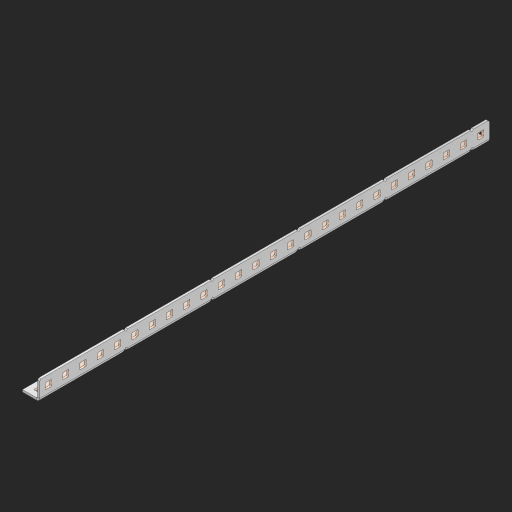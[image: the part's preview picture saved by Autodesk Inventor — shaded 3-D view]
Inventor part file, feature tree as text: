
AUTODESK INVENTOR PART (.ipt)
format: ipt  version: 2023 (Build 270158000, 158)  size: 886,272 bytes
history: native  units: in
note: dims shown in document units (in); Inventor stores cm internally (conversion verified against a paired STEP export)
features: other x57, extrude x51, sheet_metal_op x10, sketch x8, mirror x1, pattern_linear x1, chamfer x1
ambient origin geometry x8: Origin, YZ Plane, XZ Plane, XY Plane, X Axis, Y Axis, Z Axis, Center Point
bodies: Solid1 (feature_tree), Body (feature_tree)
feature tree (129):
  other  "Flange Pattern Plane"
  sheet_metal_op  "Flange Pattern"
  sheet_metal_op  "Body Pattern"
  other  "Arc Length"
  mirror  "Notch Mirror"
  pattern_linear  "Notch Pattern"  Spacing1=0.25in  [1 undecoded]
  chamfer  "End Chamfer"
  extrude  "Half Cut"  Depth=0.0625in
  sketch  "Sketch1"  dims[d0=1.5in]
  other  "Plate1"
  sketch  "Sketch2"  dims[d1=13.0in]
  other  "Plate2"
  sheet_metal_op  "Bend1"
  sheet_metal_op  "Corner1"
  sketch  "Sketch3"  dims[d2=0.0625in]
  other  "Flange Pattern Sketch"
  sketch  "Sketch7"  dims[d3=0.0625in]
  other  "Srf1"
  other  "Srf2"
  sketch  "Sketch8"  dims[d4=0.0312in]
  sketch  "Sketch9"  dims[d5=0.125in]
  other  "Srf91"
  sheet_metal_op  "Body Pattern Sketch"
  other  "Srf92"
  sketch  "Sketch13"  dims[d6=0.0625in]
  sketch  "Sketch14"  dims[d7=0.5in d8=90.0deg d9=0.0312in d10=0.25in d11=0.0625in d12=0.0625in d16=0.182in d17=0.02in d18=0.0625in d19=0.0in d20=0.25in d21=0.25in d46=0.172in d47=1.0in d48=0.0in d49=0.182in d50=0.02in d51=0.25in d52=0.25in d53=0.0625in d54=0.0in d55=0.172in d56=1.0in d57=0.0in d60=10.2362in d62=0.5in d63=0.3937in d65=0.5in d85=0.1473in d86=0.1782in d88=0.04in d89=0.0625in d90=0.0in d91=0.04in d92=0.0491in d95=2.5in d96=0.04in d97=0.25in d98=45.0deg d101=0.0in d102=2.497in d131=0.5in d132=10.2362in d134=0.5in d139=0.5in]
  other  "Srf856"
  other  "Srf1310"
  other  "Srf1311"
  other  "Srf1312"
  other  "Srf1376"
  other  "Srf1377"
  other  "Srf1728"
  other  "Srf1755"
  other  "Srf1878"
  other  "Srf1879"
  other  "Srf1880"
  other  "Srf1881"
  other  "Srf1882"
  other  "Srf1883"
  other  "Srf1884"
  other  "Srf1885"
  other  "Srf1886"
  other  "Srf1887"
  other  "Srf1888"
  other  "Srf1889"
  other  "Srf1890"
  other  "Srf1891"
  other  "Srf1892"
  other  "Srf1893"
  other  "Srf1894"
  other  "Srf1895"
  other  "Srf1896"
  other  "Srf1897"
  other  "Srf1942"
  other  "Srf1943"
  other  "Srf1944"
  other  "Srf1945"
  other  "Srf1946"
  other  "Srf1947"
  other  "Srf1948"
  other  "Srf1949"
  other  "Srf1950"
  other  "Srf1951"
  other  "Srf1952"
  other  "Srf1953"
  other  "Srf1954"
  other  "Srf1955"
  other  "Srf1956"
  other  "Srf1957"
  other  "Srf1958"
  other  "Srf1959"
  other  "Srf1960"
  other  "Srf1961"
  sheet_metal_op  "Flange Stamp"
  sheet_metal_op  "Flange Circle"
  sheet_metal_op  "Body Stamp"
  sheet_metal_op  "Body Circle"
  sheet_metal_op  "Notch"
  extrude  "ExtrusionSrf2"  Depth=0.0625in
  extrude  "ExtrusionSrf92"  Depth=0.5in
  extrude  "ExtrusionSrf856"  Depth=0.02in
  extrude  "ExtrusionSrf1310"  Depth=0.0625in
  extrude  "ExtrusionSrf1311"  TaperAngle=0.0deg  [1 undecoded]
  extrude  "ExtrusionSrf1312"  Depth=0.5in
  extrude  "ExtrusionSrf1376"  Depth=0.5in
  extrude  "ExtrusionSrf1377"  Depth=0.5in
  extrude  "ExtrusionSrf1728"  Depth=0.5in TaperAngle=0.0deg
  extrude  "ExtrusionSrf1755"  Depth=0.5in
  extrude  "ExtrusionSrf1878"  Depth=0.02in
  extrude  "ExtrusionSrf1879"  Depth=0.5in
  extrude  "ExtrusionSrf1880"  Depth=0.5in
  extrude  "ExtrusionSrf1881"  Depth=0.0625in
  extrude  "ExtrusionSrf1882"  TaperAngle=0.0deg  [1 undecoded]
  extrude  "ExtrusionSrf1883"  Depth=0.5in
  extrude  "ExtrusionSrf1884"  Depth=0.5in TaperAngle=0.0deg
  extrude  "ExtrusionSrf1885"  Depth=0.5in
  extrude  "ExtrusionSrf1886"  Depth=0.5in
  extrude  "ExtrusionSrf1887"  Depth=0.5in
  extrude  "ExtrusionSrf1888"  Depth=0.5in
  extrude  "ExtrusionSrf1889"  Depth=0.5in
  extrude  "ExtrusionSrf1890"  Depth=0.0625in
  extrude  "ExtrusionSrf1891"  TaperAngle=0.0deg  [1 undecoded]
  extrude  "ExtrusionSrf1892"  Depth=0.5in
  extrude  "ExtrusionSrf1893"  Depth=0.5in
  extrude  "ExtrusionSrf1894"  Depth=0.5in
  extrude  "ExtrusionSrf1895"  Depth=0.5in TaperAngle=45.0deg
  extrude  "ExtrusionSrf1896"  TaperAngle=0.0deg  [1 undecoded]
  extrude  "ExtrusionSrf1897"  Depth=0.5in
  extrude  "ExtrusionSrf1942"  Depth=0.5in
  extrude  "ExtrusionSrf1943"  Depth=0.5in
  extrude  "ExtrusionSrf1944"  Depth=0.5in
  extrude  "ExtrusionSrf1945"  Depth=0.5in
  extrude  "ExtrusionSrf1946"  [1 undecoded]
  extrude  "ExtrusionSrf1947"  [1 undecoded]
  extrude  "ExtrusionSrf1948"  [1 undecoded]
  extrude  "ExtrusionSrf1949"  [1 undecoded]
  extrude  "ExtrusionSrf1950"  [1 undecoded]
  extrude  "ExtrusionSrf1951"  [1 undecoded]
  extrude  "ExtrusionSrf1952"  [1 undecoded]
  extrude  "ExtrusionSrf1953"  [1 undecoded]
  extrude  "ExtrusionSrf1954"  [1 undecoded]
  extrude  "ExtrusionSrf1955"  [1 undecoded]
  extrude  "ExtrusionSrf1956"  [1 undecoded]
  extrude  "ExtrusionSrf1957"  [1 undecoded]
  extrude  "ExtrusionSrf1958"  [1 undecoded]
  extrude  "ExtrusionSrf1959"  [1 undecoded]
  extrude  "ExtrusionSrf1960"  [1 undecoded]
  extrude  "ExtrusionSrf1961"  [1 undecoded]
note: 21 required parameter values undecoded (feature->parameter linkage not recoverable at this tier; creation-order binding heuristic only, values carry confidence <= 0.55)
